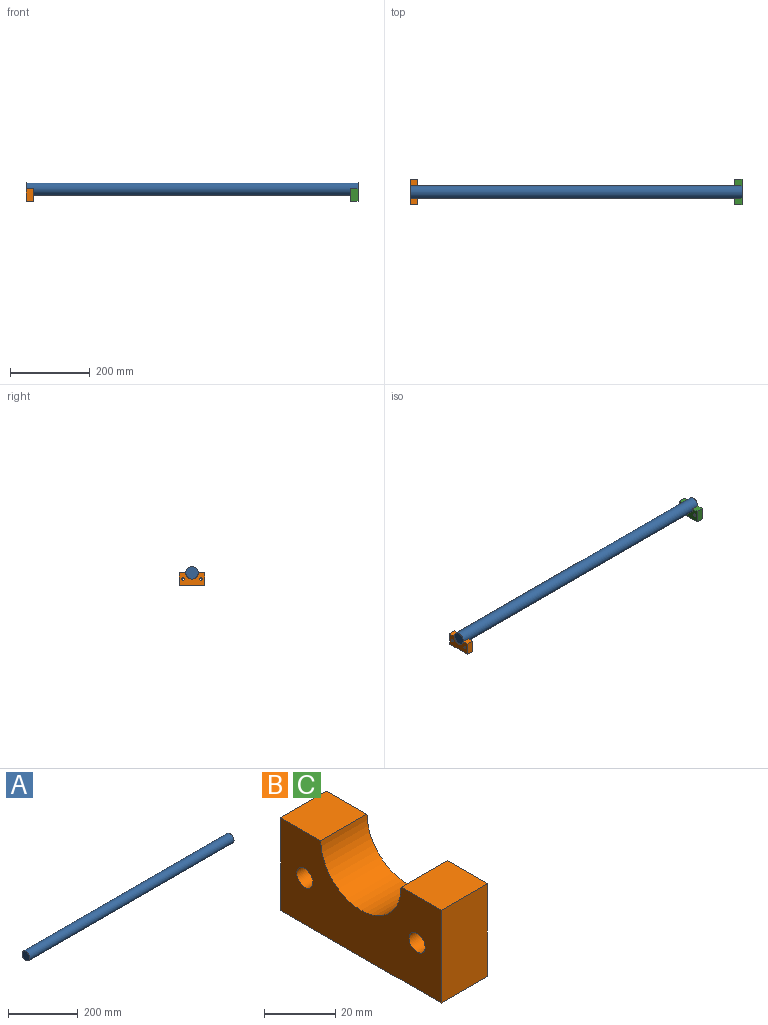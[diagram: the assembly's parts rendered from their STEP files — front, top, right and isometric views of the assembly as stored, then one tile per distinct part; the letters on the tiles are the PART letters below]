
ASSEMBLY  parts=3 mates=2
PART A: 3 faces, bbox 830.3x31.8x31.8 mm
  f0: cylinder r=15.88mm len=830.26mm, axis (1,0,0), area 82815mm2, adj f1,f2
  f1: plane 31.75x31.75mm, normal (-1,0,0), area 791.7mm2, adj f0
  f2: plane 31.75x31.75mm, normal (1,0,0), area 791.7mm2, adj f0
PART B: 10 faces, bbox 18.3x63.5x31.8 mm
  f0: plane 18.29x15.88mm, normal (0,0,1), area 290.3mm2, adj f1,f7,f8,f9
  f1: plane 31.75x18.29mm, normal (0,-1,0), area 580.6mm2, adj f0,f2,f8,f9
  f2: plane 63.5x18.29mm, normal (0,0,-1), area 1161.3mm2, adj f1,f3,f8,f9
  f3: plane 31.75x18.29mm, normal (0,1,0), area 580.6mm2, adj f2,f4,f8,f9
  f4: plane 18.29x15.88mm, normal (0,0,1), area 290.3mm2, adj f3,f7,f8,f9
  f5: cylinder r=3.17mm len=18.29mm, axis (-1,0,0), area 364.8mm2, adj f8,f9
  f6: cylinder r=3.17mm len=18.29mm, axis (-1,0,0), area 364.8mm2, adj f8,f9
  f7: cylinder r=15.88mm len=31.75mm, axis (-1,0,0), area 912.1mm2, adj f0,f4,f8,f9
  f8: plane 63.5x31.75mm, normal (1,0,0), area 1556.9mm2, adj f0,f1,f2,f3,f4,f5,f6,f7
  f9: plane 63.5x31.75mm, normal (-1,0,0), area 1556.9mm2, adj f0,f1,f2,f3,f4,f5,f6,f7
PART C: same geometry as B
PLACE A t=(16.87,-174.47,144.9)mm fixed
PLACE B t=(-796.56,-174.47,144.9)mm
PLACE C t=(16.87,-174.47,144.9)mm
MATE fastened A.f0 <-> C.f7  axis (1,0,0) through (26.02,-142.72,144.9)mm
MATE fastened C.f1 <-> B.f1  axis (0,-1,0) through (26.02,-174.47,113.15)mm
